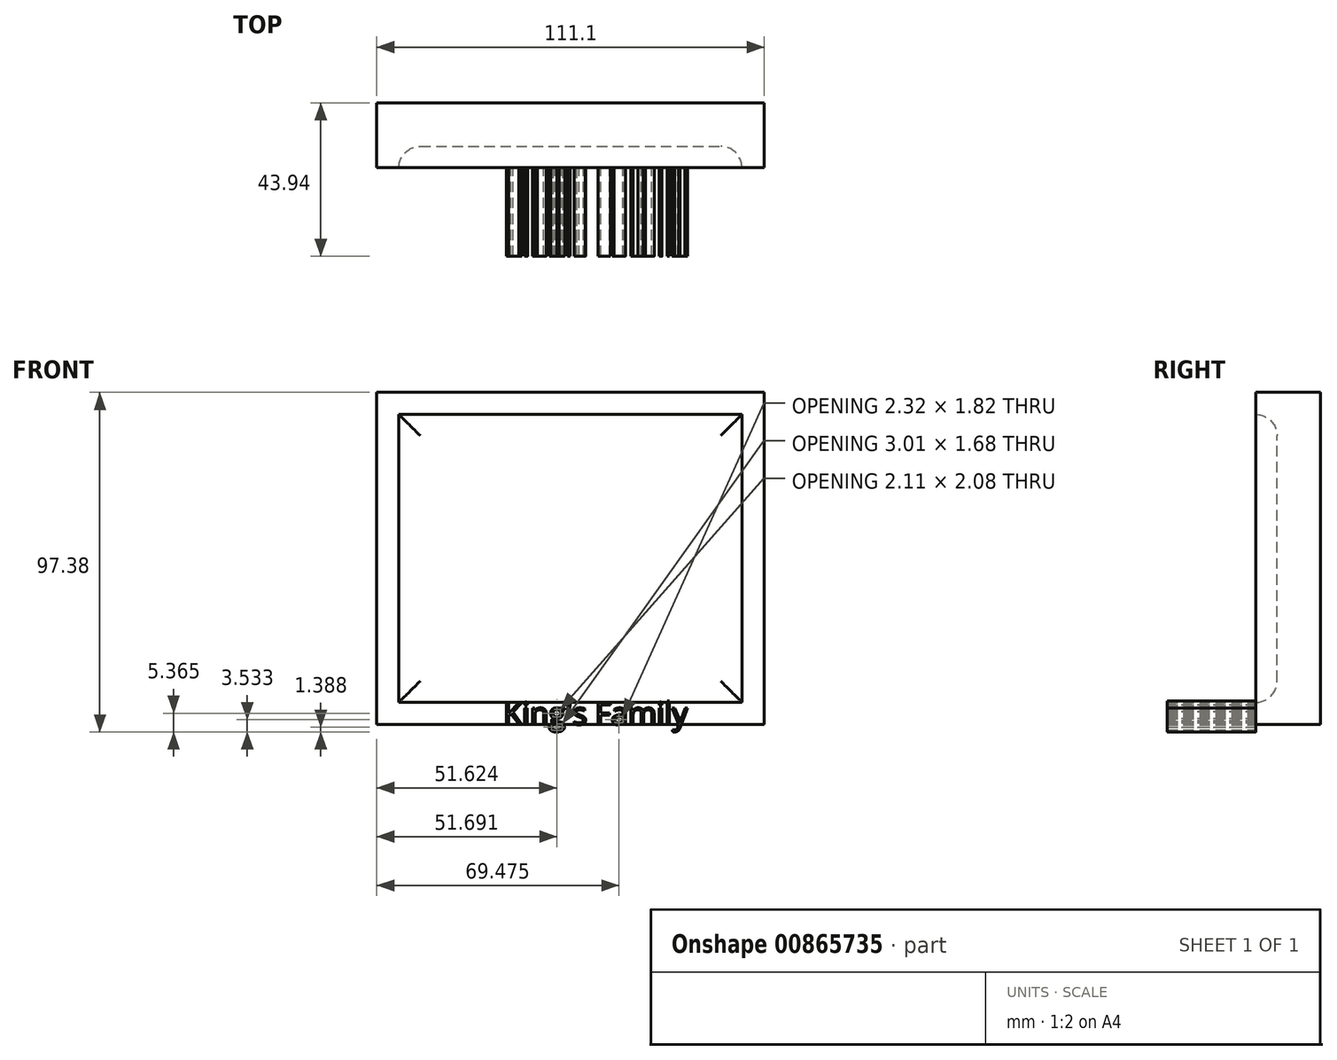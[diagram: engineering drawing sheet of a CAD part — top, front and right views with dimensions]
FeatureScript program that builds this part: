
annotation { "Feature Type Name" : "Feature", "Feature Type Description" : "" }
export const myFeature = defineFeature(function(context is Context, id is Id, definition is map)
    precondition{}
    {
        {
            var Q0;
            Q0=qCreatedBy(makeId("Front.planeOp"),FACE);
            var sketch = newSketch(context, id + "F0", { "sketchPlane" : qUnion([Q0])});
            skLineSegment(sketch, "E0", {"start": v(-57.7, 0) * mm, "end": v(-57.7, 55.11) * mm});
            skLineSegment(sketch, "E1", {"start": v(-57.7, 0) * mm, "end": v(-57.7, -40.15) * mm});
            skLineSegment(sketch, "E2", {"start": v(-57.7, -40.15) * mm, "end": v(53.39, -40.15) * mm});
            skLineSegment(sketch, "E3", {"start": v(53.39, -40.15) * mm, "end": v(53.39, 55.11) * mm});
            skLineSegment(sketch, "E4", {"start": v(-57.7, 55.11) * mm, "end": v(53.39, 55.11) * mm});
            skSolve(sketch);
        }
        {
            var Q0;
            Q0 = qSketchRegion(id + "F0", true);
            extrude(context, id + "F1", {"entities" : qUnion([Q0]), "depth" : 12.45 * mm, "offsetDistance" : 25.4 * mm});
        }
        {
            var Q0;
            Q0=makeQuery(id+"F1.opExtrude","CAP_FACE",FACE,{"disambiguationData":[OSD([sQuery(id+"F0.wireOp",EDGE,"E0"),sQuery(id+"F0.wireOp",EDGE,"E1"),sQuery(id+"F0.wireOp",EDGE,"E2"),sQuery(id+"F0.wireOp",EDGE,"E3"),sQuery(id+"F0.wireOp",EDGE,"E4")])],"isStart":false});
            var sketch = newSketch(context, id + "F2", { "sketchPlane" : qUnion([Q0])});
            skLineSegment(sketch, "E5.0", {"start": v(47.04, 48.76) * mm, "end": v(-51.36, 48.76) * mm});
            skLineSegment(sketch, "E5.1", {"start": v(47.04, -33.8) * mm, "end": v(47.04, 48.76) * mm});
            skLineSegment(sketch, "E5.2", {"start": v(-51.36, -33.8) * mm, "end": v(47.04, -33.8) * mm});
            skLineSegment(sketch, "E5.3", {"start": v(-51.36, 48.76) * mm, "end": v(-51.36, -33.8) * mm});
            skSolve(sketch);
        }
        {
            var Q0;
            Q0=makeQuery(id+"F2.imprint","IMPRINT",FACE,{"disambiguationData":[TD([[makeQuery(id+"F2.imprint","IMPRINT",EDGE,{"derivedFrom":sQuery(id+"F2.wireOp",EDGE,"E5.0")}),-1.0]])]});
            extrude(context, id + "F3", {"entities" : qUnion([Q0]), "operationType" : NewBodyOperationType.ADD, "depth" : 6.1 * mm, "offsetDistance" : 25.4 * mm});
        }
        {
            var Q0;
            Q0=makeQuery(id+"F1.opExtrude","CAP_FACE",FACE,{"disambiguationData":[OSD([sQuery(id+"F0.wireOp",EDGE,"E0"),sQuery(id+"F0.wireOp",EDGE,"E1"),sQuery(id+"F0.wireOp",EDGE,"E2"),sQuery(id+"F0.wireOp",EDGE,"E3"),sQuery(id+"F0.wireOp",EDGE,"E4")])],"isStart":false});
            fillet(context, id + "F4", {"entities" : qUnion([Q0]), "radius" : 6.13 * mm, "tangentPropagation" : true, "allowEdgeOverflow" : false});
        }
        {
            var Q0;
            Q0=makeQuery(id+"F3.opExtrude","CAP_FACE",FACE,{"disambiguationData":[OSD([sQuery(id+"F0.wireOp",EDGE,"E0"),sQuery(id+"F0.wireOp",EDGE,"E1"),sQuery(id+"F0.wireOp",EDGE,"E2"),sQuery(id+"F0.wireOp",EDGE,"E3"),sQuery(id+"F0.wireOp",EDGE,"E4"),sQuery(id+"F2.wireOp",EDGE,"E5.0"),sQuery(id+"F2.wireOp",EDGE,"E5.1"),sQuery(id+"F2.wireOp",EDGE,"E5.2"),sQuery(id+"F2.wireOp",EDGE,"E5.3")])],"isStart":false});
            var sketch = newSketch(context, id + "F5", { "sketchPlane" : qUnion([Q0])});
            skText(sketch, "E6", { "text": "King\'s Family", "fontName": "OpenSans-Regular.ttf"});
            const initialGuessF5  = {"E6": [-0.02144, -0.04015, 1, 0, 0.00635]};
            skSetInitialGuess(sketch, initialGuessF5);
            skSolve(sketch);
        }
        {
            var Q0;
            Q0 = qSketchRegion(id + "F5", true);
            extrude(context, id + "F6", {"entities" : qUnion([Q0]), "depth" : 25.4 * mm, "offsetDistance" : 25.4 * mm});
        }
    });
